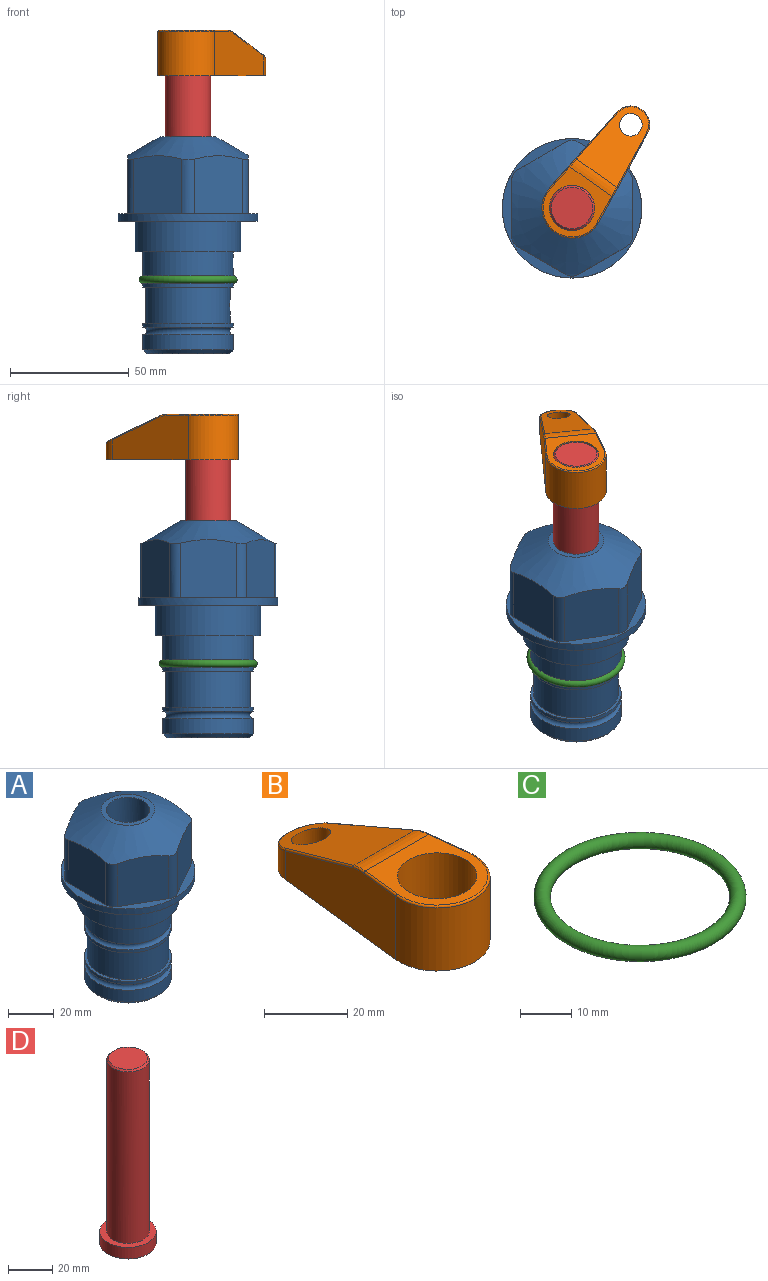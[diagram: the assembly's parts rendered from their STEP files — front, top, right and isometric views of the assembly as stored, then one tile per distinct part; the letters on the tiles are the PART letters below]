
ASSEMBLY  parts=4 mates=2
PART A: 36 faces, bbox 58.7x58.7x91.2 mm
  f0: cylinder r=17.78mm len=35.56mm, axis (0,0,1), area 1670.8mm2, adj f23,f24,f31
  f1: cylinder r=19.05mm len=38.1mm, axis (0,0,1), area 1191.9mm2, adj f26,f27,f30
  f2: plane 58.66x58.66mm, normal (0,0,-1), area 1150.6mm2, adj f3,f28
  f3: cylinder r=29.33mm len=58.66mm, axis (0,0,-1), area 585.1mm2, adj f2,f4
  f4: plane 58.66x58.66mm, normal (0,0,1), area 475.9mm2, adj f3,f5,f6,f7,f8,f9,f10,f11
  f5: plane 24.5x20.32mm, normal (-0.5,0.87,0), area 562.8mm2, adj f4,f15,f16,f17
  f6: plane 24.5x20.32mm, normal (0.5,0.87,0), area 562.8mm2, adj f4,f14,f15,f17
  f7: plane 24.5x23.48mm, normal (1,0,0), area 562.8mm2, adj f4,f13,f14,f17
  f8: plane 24.5x20.32mm, normal (0.5,-0.87,0), area 562.8mm2, adj f4,f12,f13,f17
  f9: plane 24.5x20.32mm, normal (-0.5,-0.87,0), area 562.8mm2, adj f4,f11,f12,f17
  f10: plane 24.5x23.48mm, normal (-1,0,0), area 562.8mm2, adj f4,f11,f16,f17
  f11: cylinder r=5.08mm len=23.01mm, axis (0,0,-1), area 121.2mm2, adj f4,f9,f10,f17
  f12: cylinder r=5.08mm len=23.01mm, axis (0,0,-1), area 121.2mm2, adj f4,f8,f9,f17
  f13: cylinder r=5.08mm len=23.01mm, axis (0,0,-1), area 121.2mm2, adj f4,f7,f8,f17
  f14: cylinder r=5.08mm len=23.01mm, axis (0,0,-1), area 121.2mm2, adj f4,f6,f7,f17
  f15: cylinder r=5.08mm len=23.01mm, axis (0,0,-1), area 121.2mm2, adj f4,f5,f6,f17
  f16: cylinder r=5.08mm len=23.01mm, axis (0,0,-1), area 121.2mm2, adj f4,f5,f10,f17
  f17: cone r=11.73mm half-angle=60deg, axis (0,0,-1), area 2071.8mm2, adj f5,f6,f7,f8,f9,f10,f11,f12
  f18: plane 23.46x23.46mm, normal (0,0,1), area 147.4mm2, adj f17,f35
  f19: plane 34.93x34.93mm, normal (0,0,-1), area 958mm2, adj f29
  f20: cylinder r=19.05mm len=38.1mm, axis (0,0,1), area 760.1mm2, adj f21,f29
  f21: torus R=19.05mm, axis (0,0,1), area 565.3mm2, adj f20,f22
  f22: cylinder r=19.05mm len=38.1mm, axis (0,0,1), area 190mm2, adj f21,f23
  f23: plane 38.1x38.1mm, normal (0,0,1), area 146.9mm2, adj f0,f22
  f24: plane 38.1x38.1mm, normal (0,0,-1), area 146.9mm2, adj f0,f25
  f25: cylinder r=19.05mm len=38.1mm, axis (0,0,1), area 190mm2, adj f24,f26
  f26: torus R=19.05mm, axis (0,0,1), area 565.3mm2, adj f1,f25
  f27: plane 44.45x44.45mm, normal (0,0,-1), area 411.7mm2, adj f1,f28
  f28: cylinder r=22.23mm len=44.45mm, axis (0,0,1), area 1773.5mm2, adj f2,f27
  f29: cone r=19.05mm half-angle=45deg, axis (0,0,1), area 257.5mm2, adj f19,f20
  f30: cylinder r=3.17mm len=6.75mm, axis (-1,0,0), area 128mm2, adj f1,f33
  f31: cylinder r=3.17mm len=6.35mm, axis (-1,0,0), area 102.5mm2, adj f0,f33
  f32: plane 25.4x25.4mm, normal (0,0,1), area 506.7mm2, adj f33
  f33: cylinder r=12.7mm len=66.42mm, axis (0,0,-1), area 5236.2mm2, adj f30,f31,f32,f34
  f34: cone r=9.53mm half-angle=30deg, axis (0,0,-1), area 443.4mm2, adj f33,f35
  f35: cylinder r=9.53mm len=19.05mm, axis (0,0,-1), area 849mm2, adj f18,f34
PART B: 44 faces, bbox 27.5x64.5x19.1 mm
  f0: plane 2.3x0.95mm, normal (0,0,-1), area 1mm2, adj f25,f30,f34
  f1: plane 63.5x25.4mm, normal (0,0,-1), area 561.7mm2, adj f2,f3,f4,f5,f6,f7,f19,f20
  f2: cylinder r=12.7mm len=25.4mm, axis (0,0,-1), area 792.2mm2, adj f1,f3,f5,f13
  f3: plane 42.33x18.54mm, normal (0.99,0.11,0), area 647mm2, adj f1,f2,f4,f11,f12,f14
  f4: cylinder r=7.94mm len=15.78mm, axis (0,0,-1), area 158.6mm2, adj f1,f3,f5,f16
  f5: plane 42.33x18.54mm, normal (-0.99,0.11,0), area 647mm2, adj f1,f2,f4,f15,f17,f18
  f6: cylinder r=9.53mm len=19.05mm, axis (0,0,-1), area 1140.1mm2, adj f1,f8
  f7: cylinder r=4.76mm len=10.98mm, axis (0,0,-1), area 276.1mm2, adj f1,f9
  f8: plane 25.83x24.38mm, normal (0,0,1), area 262.2mm2, adj f6,f10,f11,f13,f15
  f9: plane 32.49x20.55mm, normal (0,0.34,0.94), area 489.9mm2, adj f7,f10,f14,f16,f18
  f10: cylinder r=12.7mm len=21.49mm, axis (-1,0,0), area 93.2mm2, adj f8,f9,f12,f17
  f11: cylinder r=0.51mm len=12.34mm, axis (0.11,-0.99,0), area 9.9mm2, adj f3,f8,f12,f13
  f12: bspline ~7.62x1.64mm, area 3.5mm2, adj f3,f10,f11,f14
  f13: torus R=12.19mm, axis (0,0,1), area 33.6mm2, adj f2,f8,f11,f15
  f14: cylinder r=0.51mm len=26.01mm, axis (0.1,-0.93,0.34), area 21.6mm2, adj f3,f9,f12,f16
  f15: cylinder r=0.51mm len=12.34mm, axis (0.11,0.99,0), area 9.9mm2, adj f5,f8,f13,f17
  f16: bspline ~15.78x7.05mm, area 15.7mm2, adj f4,f9,f14,f18
  f17: bspline ~7.62x1.64mm, area 3.5mm2, adj f5,f10,f15,f18
  f18: cylinder r=0.51mm len=26.01mm, axis (0.1,0.93,-0.34), area 21.6mm2, adj f5,f9,f16,f17
  f19: plane 21.6x14.29mm, normal (-0.99,-0.11,0), area 242.6mm2, adj f1,f26,f28,f34,f36,f38
  f20: plane 21.6x14.29mm, normal (0.99,-0.11,0), area 242.6mm2, adj f1,f27,f29,f37,f39,f41
  f21: cylinder r=12.7mm len=14.29mm, axis (0,0,-1), area 173.2mm2, adj f1,f26,f27,f30,f31,f33
  f22: cylinder r=7.94mm len=7.63mm, axis (0,0,-1), area 53.8mm2, adj f1,f28,f29,f42
  f23: plane 2.3x0.95mm, normal (0,0,-1), area 1mm2, adj f25,f33,f37
  f24: plane 17.94x12.32mm, normal (0,-0.34,-0.94), area 191.2mm2, adj f25,f38,f41,f42
  f25: cylinder r=9.53mm len=12.93mm, axis (-1,0,0), area 37.5mm2, adj f0,f23,f24,f31,f36,f39
  f26: cylinder r=1.59mm len=14.29mm, axis (0,0,-1), area 49mm2, adj f1,f19,f21,f32
  f27: cylinder r=1.59mm len=14.29mm, axis (0,0,-1), area 49mm2, adj f1,f20,f21,f35
  f28: cylinder r=1.59mm len=7.28mm, axis (0,0,-1), area 22.1mm2, adj f1,f19,f22,f40
  f29: cylinder r=1.59mm len=7.28mm, axis (0,0,-1), area 22.1mm2, adj f1,f20,f22,f43
  f30: torus R=14.29mm, axis (0,0,1), area 5.8mm2, adj f0,f21,f31,f32
  f31: bspline ~11.06x2.73mm, area 20.8mm2, adj f21,f25,f30,f33
  f32: sphere r=1.59mm, area 5.4mm2, adj f26,f30,f34
  f33: torus R=14.29mm, axis (0,0,1), area 5.8mm2, adj f21,f23,f31,f35
  f34: cylinder r=1.59mm len=1.68mm, axis (-0.11,0.99,0), area 2.4mm2, adj f0,f19,f32,f36
  f35: sphere r=1.59mm, area 5.4mm2, adj f27,f33,f37
  f36: bspline ~5.82x2.33mm, area 7.7mm2, adj f19,f25,f34,f38
  f37: cylinder r=1.59mm len=1.68mm, axis (0.11,0.99,0), area 2.4mm2, adj f20,f23,f35,f39
  f38: cylinder r=1.59mm len=18.33mm, axis (0.1,-0.93,0.34), area 46.7mm2, adj f19,f24,f36,f40
  f39: bspline ~5.82x2.33mm, area 7.7mm2, adj f20,f25,f37,f41
  f40: sphere r=1.59mm, area 3.6mm2, adj f28,f38,f42
  f41: cylinder r=1.59mm len=18.33mm, axis (0.1,0.93,-0.34), area 46.7mm2, adj f20,f24,f39,f43
  f42: bspline ~8.31x1.84mm, area 15.3mm2, adj f22,f24,f40,f43
  f43: sphere r=1.59mm, area 3.6mm2, adj f29,f41,f42
PART C: 1 faces, bbox 44.7x44.7x3.2 mm
  f0: torus R=19.05mm, axis (0,0,1), area 1193.9mm2
PART D: 6 faces, bbox 25.4x25.4x101.6 mm
  f0: plane 17.46x17.46mm, normal (0,0,1), area 239.5mm2, adj f5
  f1: plane 25.4x25.4mm, normal (0,0,-1), area 506.7mm2, adj f2
  f2: cylinder r=12.7mm len=25.4mm, axis (0,0,1), area 506.7mm2, adj f1,f3
  f3: plane 25.4x25.4mm, normal (0,0,1), area 221.7mm2, adj f2,f4
  f4: cylinder r=9.53mm len=94.46mm, axis (0,0,1), area 5653mm2, adj f3,f5
  f5: cone r=8.73mm half-angle=45deg, axis (0,0,-1), area 64.4mm2, adj f0,f4
PLACE A at identity fixed
PLACE B rot(axis=(0,0,-1),35.2deg) t=(0,0,61.29)mm
PLACE C at identity
PLACE D rot(axis=(0,0,-1),35.2deg) t=(0,0,6.68)mm
MATE cylindrical D.f2 <-> A.f0  axis (0,0,1) through (0,0,32.32)mm
MATE fastened B.f2 <-> D.f2  axis (0,0,-1) through (0,0,80.34)mm
